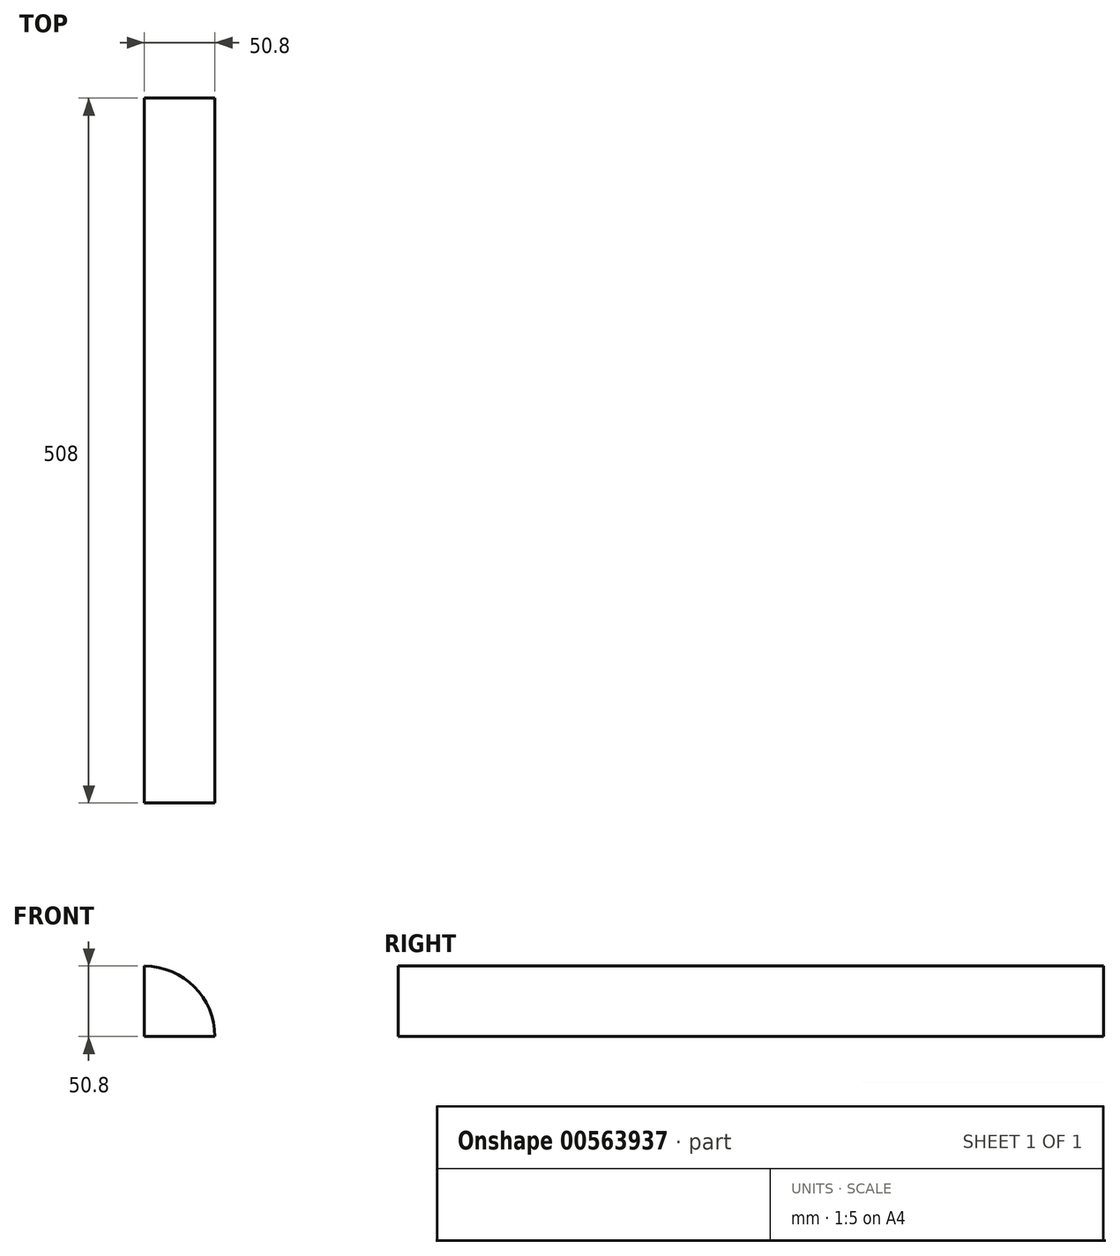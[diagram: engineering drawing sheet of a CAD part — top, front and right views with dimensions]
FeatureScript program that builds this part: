
annotation { "Feature Type Name" : "Feature", "Feature Type Description" : "" }
export const myFeature = defineFeature(function(context is Context, id is Id, definition is map)
    precondition{}
    {
        {
            var Q0;
            Q0=qCreatedBy(makeId("Front.planeOp"),FACE);
            var sketch = newSketch(context, id + "F0", { "sketchPlane" : qUnion([Q0])});
            skLineSegment(sketch, "E0", {"start": v(0, 0) * mm, "end": v(0, 50.8) * mm});
            skLineSegment(sketch, "E1", {"start": v(0, 0) * mm, "end": v(50.8, 0) * mm});
            skArc(sketch, "E2", {"start": v(50.8, 0) * mm, "mid": v(35.92, 35.92) * mm, "end": v(0, 50.8) * mm});
            skSolve(sketch);
        }
        {
            var Q0;
            Q0 = qSketchRegion(id + "F0", true);
            extrude(context, id + "F1", {"entities" : qUnion([Q0]), "depth" : 508 * mm, "offsetDistance" : 25.4 * mm, "symmetric" : true});
        }
    });
